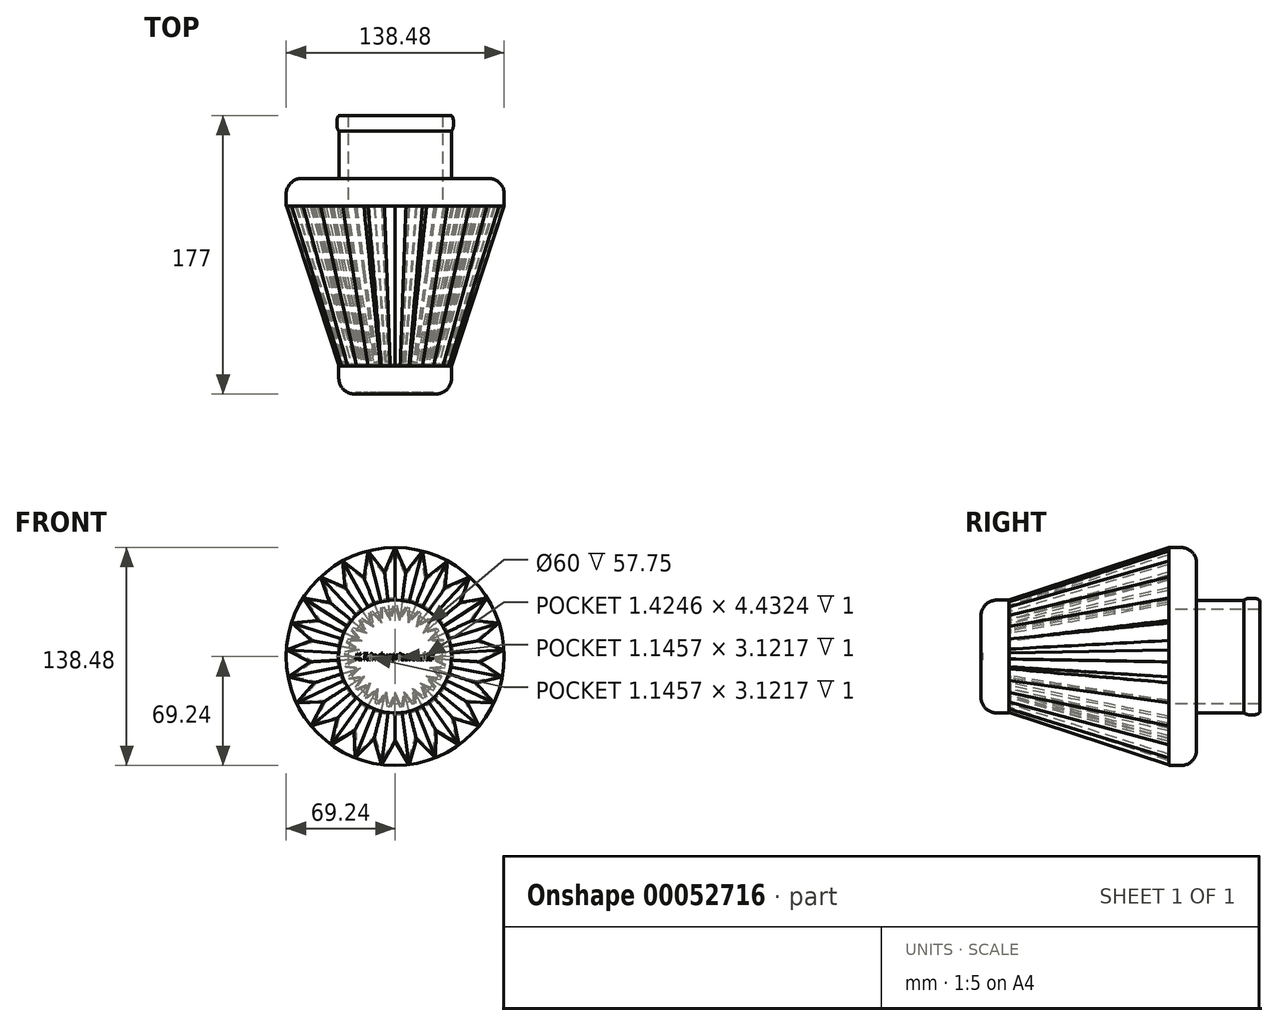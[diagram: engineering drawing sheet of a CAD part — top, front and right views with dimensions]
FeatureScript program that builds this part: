
annotation { "Feature Type Name" : "Feature", "Feature Type Description" : "" }
export const myFeature = defineFeature(function(context is Context, id is Id, definition is map)
    precondition{}
    {
        {
            var Q0;
            Q0=qCreatedBy(makeId("Front.planeOp"),FACE);
            var sketch = newSketch(context, id + "F0", { "sketchPlane" : qUnion([Q0])});
            skLineSegment(sketch, "E0", {"start": v(0, 0) * mm, "end": v(0, 69.24) * mm, "construction": true});
            skLineSegment(sketch, "E1", {"start": v(0, 69.24) * mm, "end": v(-8.68, 49.24) * mm});
            skLineSegment(sketch, "E2", {"start": v(-8.68, 49.24) * mm, "end": v(0, 0) * mm});
            skLineSegment(sketch, "E3.MirrorCS", {"start": v(0, 69.24) * mm, "end": v(8.68, 49.24) * mm});
            skLineSegment(sketch, "E4.MirrorCS", {"start": v(8.68, 49.24) * mm, "end": v(0, 0) * mm});
            skSolve(sketch);
        }
        {
            var Q0;
            Q0=qCreatedBy(makeId("Front.planeOp"),FACE);
            cPlane(context, id + "F1", {"entities" : qUnion([Q0]), "cplaneType" : CPlaneType.OFFSET, "offset" : 101.5 * mm, "width" : 150 * mm, "height" : 150 * mm});
        }
        {
            var Q0;
            Q0=qCreatedBy(id+"F1.planeOp",FACE);
            var sketch = newSketch(context, id + "F2", { "sketchPlane" : qUnion([Q0])});
            skLineSegment(sketch, "E5.0", {"start": v(0, 0) * mm, "end": v(0, 69.24) * mm, "construction": true});
            skLineSegment(sketch, "E6", {"start": v(0, 0) * mm, "end": v(-3.26, 24.79) * mm});
            skLineSegment(sketch, "E7", {"start": v(-3.26, 24.79) * mm, "end": v(0, 35.81) * mm});
            skLineSegment(sketch, "E8.MirrorCS", {"start": v(3.26, 24.79) * mm, "end": v(0, 35.81) * mm});
            skLineSegment(sketch, "E9.MirrorCS", {"start": v(0, 0) * mm, "end": v(3.26, 24.79) * mm});
            skSolve(sketch);
        }
        {
            var Q0;
            Q0=makeQuery(id+"F0.imprint","IMPRINT",FACE,{"disambiguationData":[TD([[makeQuery(id+"F0.imprint","IMPRINT",EDGE,{"derivedFrom":sQuery(id+"F0.wireOp",EDGE,"E1")}),1.0]])]});
            var Q1;
            Q1=makeQuery(id+"F2.imprint","IMPRINT",FACE,{"disambiguationData":[TD([[makeQuery(id+"F2.imprint","IMPRINT",EDGE,{"derivedFrom":sQuery(id+"F2.wireOp",EDGE,"E6")}),-1.0]])]});
            loft(context, id + "F3", {"sheetProfilesArray" : [{ "sheetProfileEntities" : qUnion([Q0]) }, { "sheetProfileEntities" : qUnion([Q1]) }]});
        }
        {
            var Q0;
            Q0=qCreatedBy(makeId("Right.planeOp"),FACE);
            var sketch = newSketch(context, id + "F4", { "sketchPlane" : qUnion([Q0])});
            skLineSegment(sketch, "E10", {"start": v(0, 0) * mm, "end": v(-101.5, 0) * mm, "construction": true});
            skSolve(sketch);
        }
        {
            var Q0;
            Q0=makeQuery(id+"F3.opLoft","SWEPT_BODY",BODY,{"disambiguationData":[OSD([makeQuery(id+"F0.imprint","IMPRINT",FACE,{"disambiguationData":[TD([[makeQuery(id+"F0.imprint","IMPRINT",EDGE,{"derivedFrom":sQuery(id+"F0.wireOp",EDGE,"E1")}),1.0]])]}),makeQuery(id+"F2.imprint","IMPRINT",FACE,{"disambiguationData":[TD([[makeQuery(id+"F2.imprint","IMPRINT",EDGE,{"derivedFrom":sQuery(id+"F2.wireOp",EDGE,"E6")}),-1.0]])]})])]});
            var Q1;
            Q1=makeQuery(id+"F3.opLoft","SWEPT_FACE",FACE,{"disambiguationData":[OSD([sQuery(id+"F0.wireOp",EDGE,"E2"),sQuery(id+"F0.wireOp",EDGE,"E3.MirrorCS"),sQuery(id+"F0.wireOp",EDGE,"E4.MirrorCS"),sQuery(id+"F2.wireOp",EDGE,"E6"),sQuery(id+"F2.wireOp",EDGE,"E8.MirrorCS"),sQuery(id+"F2.wireOp",EDGE,"E9.MirrorCS")])]});
            var Q2;
            Q2=sQuery(id+"F4.wireOp",EDGE,"E10");
            circularPattern(context, id + "F5", {"operationType" : NewBodyOperationType.ADD, "entities" : qUnion([Q0]), "axis" : qUnion([Q2]), "angle" : 360 * degree, "instanceCount" : round(25), "oppositeDirection" : true, "equalSpace" : true});
        }
        {
            var Q0;
            {var subQ0=makeQuery(id+"F3.opLoft","CAP_FACE",FACE,{"disambiguationData":[OSD([makeQuery(id+"F2.imprint","IMPRINT",FACE,{"disambiguationData":[TD([[makeQuery(id+"F2.imprint","IMPRINT",EDGE,{"derivedFrom":sQuery(id+"F2.wireOp",EDGE,"E6")}),-1.0]])]})])],"isStart":true});Q0=makeQuery(id+"F5.boolean.opBoolean","MERGE",FACE,{"derivedFrom":[subQ0,makeQuery(id+"F5.opPattern","COPY",FACE,{"derivedFrom":subQ0,"instanceName":"1"}),makeQuery(id+"F5.opPattern","COPY",FACE,{"derivedFrom":subQ0,"instanceName":"2"}),makeQuery(id+"F5.opPattern","COPY",FACE,{"derivedFrom":subQ0,"instanceName":"3"}),makeQuery(id+"F5.opPattern","COPY",FACE,{"derivedFrom":subQ0,"instanceName":"4"}),makeQuery(id+"F5.opPattern","COPY",FACE,{"derivedFrom":subQ0,"instanceName":"5"}),makeQuery(id+"F5.opPattern","COPY",FACE,{"derivedFrom":subQ0,"instanceName":"6"}),makeQuery(id+"F5.opPattern","COPY",FACE,{"derivedFrom":subQ0,"instanceName":"7"}),makeQuery(id+"F5.opPattern","COPY",FACE,{"derivedFrom":subQ0,"instanceName":"8"}),makeQuery(id+"F5.opPattern","COPY",FACE,{"derivedFrom":subQ0,"instanceName":"9"}),makeQuery(id+"F5.opPattern","COPY",FACE,{"derivedFrom":subQ0,"instanceName":"10"}),makeQuery(id+"F5.opPattern","COPY",FACE,{"derivedFrom":subQ0,"instanceName":"11"}),makeQuery(id+"F5.opPattern","COPY",FACE,{"derivedFrom":subQ0,"instanceName":"12"}),makeQuery(id+"F5.opPattern","COPY",FACE,{"derivedFrom":subQ0,"instanceName":"13"}),makeQuery(id+"F5.opPattern","COPY",FACE,{"derivedFrom":subQ0,"instanceName":"14"}),makeQuery(id+"F5.opPattern","COPY",FACE,{"derivedFrom":subQ0,"instanceName":"15"}),makeQuery(id+"F5.opPattern","COPY",FACE,{"derivedFrom":subQ0,"instanceName":"16"}),makeQuery(id+"F5.opPattern","COPY",FACE,{"derivedFrom":subQ0,"instanceName":"17"}),makeQuery(id+"F5.opPattern","COPY",FACE,{"derivedFrom":subQ0,"instanceName":"18"}),makeQuery(id+"F5.opPattern","COPY",FACE,{"derivedFrom":subQ0,"instanceName":"19"}),makeQuery(id+"F5.opPattern","COPY",FACE,{"derivedFrom":subQ0,"instanceName":"20"}),makeQuery(id+"F5.opPattern","COPY",FACE,{"derivedFrom":subQ0,"instanceName":"21"}),makeQuery(id+"F5.opPattern","COPY",FACE,{"derivedFrom":subQ0,"instanceName":"22"}),makeQuery(id+"F5.opPattern","COPY",FACE,{"derivedFrom":subQ0,"instanceName":"23"}),makeQuery(id+"F5.opPattern","COPY",FACE,{"derivedFrom":subQ0,"instanceName":"24"})]});}
            var Q1;
            {var subQ0=makeQuery(id+"F3.opLoft","CAP_FACE",FACE,{"disambiguationData":[OSD([makeQuery(id+"F0.imprint","IMPRINT",FACE,{"disambiguationData":[TD([[makeQuery(id+"F0.imprint","IMPRINT",EDGE,{"derivedFrom":sQuery(id+"F0.wireOp",EDGE,"E1")}),1.0]])]})])],"isStart":true});Q1=makeQuery(id+"F5.boolean.opBoolean","MERGE",FACE,{"derivedFrom":[subQ0,makeQuery(id+"F5.opPattern","COPY",FACE,{"derivedFrom":subQ0,"instanceName":"1"}),makeQuery(id+"F5.opPattern","COPY",FACE,{"derivedFrom":subQ0,"instanceName":"2"}),makeQuery(id+"F5.opPattern","COPY",FACE,{"derivedFrom":subQ0,"instanceName":"3"}),makeQuery(id+"F5.opPattern","COPY",FACE,{"derivedFrom":subQ0,"instanceName":"4"}),makeQuery(id+"F5.opPattern","COPY",FACE,{"derivedFrom":subQ0,"instanceName":"5"}),makeQuery(id+"F5.opPattern","COPY",FACE,{"derivedFrom":subQ0,"instanceName":"6"}),makeQuery(id+"F5.opPattern","COPY",FACE,{"derivedFrom":subQ0,"instanceName":"7"}),makeQuery(id+"F5.opPattern","COPY",FACE,{"derivedFrom":subQ0,"instanceName":"8"}),makeQuery(id+"F5.opPattern","COPY",FACE,{"derivedFrom":subQ0,"instanceName":"9"}),makeQuery(id+"F5.opPattern","COPY",FACE,{"derivedFrom":subQ0,"instanceName":"10"}),makeQuery(id+"F5.opPattern","COPY",FACE,{"derivedFrom":subQ0,"instanceName":"11"}),makeQuery(id+"F5.opPattern","COPY",FACE,{"derivedFrom":subQ0,"instanceName":"12"}),makeQuery(id+"F5.opPattern","COPY",FACE,{"derivedFrom":subQ0,"instanceName":"13"}),makeQuery(id+"F5.opPattern","COPY",FACE,{"derivedFrom":subQ0,"instanceName":"14"}),makeQuery(id+"F5.opPattern","COPY",FACE,{"derivedFrom":subQ0,"instanceName":"15"}),makeQuery(id+"F5.opPattern","COPY",FACE,{"derivedFrom":subQ0,"instanceName":"16"}),makeQuery(id+"F5.opPattern","COPY",FACE,{"derivedFrom":subQ0,"instanceName":"17"}),makeQuery(id+"F5.opPattern","COPY",FACE,{"derivedFrom":subQ0,"instanceName":"18"}),makeQuery(id+"F5.opPattern","COPY",FACE,{"derivedFrom":subQ0,"instanceName":"19"}),makeQuery(id+"F5.opPattern","COPY",FACE,{"derivedFrom":subQ0,"instanceName":"20"}),makeQuery(id+"F5.opPattern","COPY",FACE,{"derivedFrom":subQ0,"instanceName":"21"}),makeQuery(id+"F5.opPattern","COPY",FACE,{"derivedFrom":subQ0,"instanceName":"22"}),makeQuery(id+"F5.opPattern","COPY",FACE,{"derivedFrom":subQ0,"instanceName":"23"}),makeQuery(id+"F5.opPattern","COPY",FACE,{"derivedFrom":subQ0,"instanceName":"24"})]});}
            shell(context, id + "F6", {"entities" : qUnion([Q0, Q1]), "thickness" : 1 * mm});
        }
        {
            var Q0;
            Q0=qCreatedBy(makeId("Front.planeOp"),FACE);
            var sketch = newSketch(context, id + "F7", { "sketchPlane" : qUnion([Q0])});
            skCircle(sketch, "E11", {"center": v(0, 0) * mm, "radius": 69.24 * mm});
            skCircle(sketch, "E12", {"center": v(0, 0) * mm, "radius": 30 * mm});
            skSolve(sketch);
        }
        {
            var Q0;
            Q0=qSketchRegion(id+"F7",true);
            extrude(context, id + "F8", {"entities" : qUnion([Q0]), "oppositeDirection" : true, "depth" : 17.75 * mm});
        }
        {
            var Q0;
            Q0=qCreatedBy(id+"F1.planeOp",FACE);
            var sketch = newSketch(context, id + "F9", { "sketchPlane" : qUnion([Q0])});
            skCircle(sketch, "E13", {"center": v(0, 0) * mm, "radius": 35.81 * mm});
            skSolve(sketch);
        }
        {
            var Q0;
            Q0=makeQuery(id+"F9.imprint","IMPRINT",FACE,{"disambiguationData":[TD([[makeQuery(id+"F9.imprint","IMPRINT",EDGE,{"derivedFrom":sQuery(id+"F9.wireOp",EDGE,"E13")}),1.0]])]});
            extrude(context, id + "F10", {"entities" : qUnion([Q0]), "depth" : 17.75 * mm});
        }
        {
            var Q0;
            Q0=makeQuery(id+"F8.opExtrude","CAP_FACE",FACE,{"disambiguationData":[OSD([sQuery(id+"F7.wireOp",EDGE,"E11"),sQuery(id+"F7.wireOp",EDGE,"E12")])],"isStart":false});
            var sketch = newSketch(context, id + "F11", { "sketchPlane" : qUnion([Q0])});
            skCircle(sketch, "E14", {"center": v(0, 0) * mm, "radius": 35.76 * mm});
            skSolve(sketch);
        }
        {
            var Q0;
            Q0=makeQuery(id+"F11.imprint","IMPRINT",FACE,{"disambiguationData":[TD([[makeQuery(id+"F11.imprint","IMPRINT",EDGE,{"derivedFrom":sQuery(id+"F11.wireOp",EDGE,"E14")}),1.0]])]});
            extrude(context, id + "F12", {"entities" : qUnion([Q0]), "operationType" : NewBodyOperationType.ADD, "depth" : 35 * mm});
        }
        {
            var Q0;
            Q0=makeQuery(id+"F12.opExtrude","CAP_FACE",FACE,{"disambiguationData":[OSD([sQuery(id+"F7.wireOp",EDGE,"E12"),sQuery(id+"F11.wireOp",EDGE,"E14")])],"isStart":false});
            var sketch = newSketch(context, id + "F13", { "sketchPlane" : qUnion([Q0])});
            skCircle(sketch, "E15", {"center": v(0, 0) * mm, "radius": 37 * mm});
            skSolve(sketch);
        }
        {
            var Q0;
            Q0=makeQuery(id+"F13.imprint","IMPRINT",FACE,{"disambiguationData":[TD([[makeQuery(id+"F13.imprint","IMPRINT",EDGE,{"derivedFrom":sQuery(id+"F13.wireOp",EDGE,"E15")}),1.0]])]});
            extrude(context, id + "F14", {"entities" : qUnion([Q0]), "operationType" : NewBodyOperationType.ADD, "depth" : 10 * mm, "symmetric" : true});
        }
        {
            var Q0;
            Q0=makeQuery(id+"F10.opExtrude","CAP_FACE",FACE,{"disambiguationData":[OSD([sQuery(id+"F9.wireOp",EDGE,"E13")])],"isStart":false});
            var sketch = newSketch(context, id + "F15", { "sketchPlane" : qUnion([Q0])});
            skText(sketch, "E16", { "text": "K.T.industries.co.ltd", "fontName": "OpenSans-Italic.ttf"});
            const initialGuessF15  = {"E16": [-0.02549, -0.00219, 1, 0, 0.0042]};
            skSetInitialGuess(sketch, initialGuessF15);
            skSolve(sketch);
        }
        {
            var Q0;
            Q0=qSketchRegion(id+"F15",true);
            extrude(context, id + "F16", {"entities" : qUnion([Q0]), "operationType" : NewBodyOperationType.REMOVE, "oppositeDirection" : true, "depth" : 1 * mm});
        }
        {
            var Q0;
            Q0=makeQuery(id+"F10.opExtrude","CAP_EDGE",EDGE,{"disambiguationData":[OSD([sQuery(id+"F9.wireOp",EDGE,"E13")])],"isStart":false});
            var Q1;
            Q1=makeQuery(id+"F8.opExtrude","CAP_EDGE",EDGE,{"disambiguationData":[OSD([sQuery(id+"F7.wireOp",EDGE,"E11")])],"isStart":false});
            fillet(context, id + "F17", {"entities" : qUnion([Q0, Q1]), "radius" : 10 * mm, "tangentPropagation" : true, "allowEdgeOverflow" : false});
        }
        {
            var Q0;
            Q0=makeQuery(id+"F14.opExtrude","CAP_EDGE",EDGE,{"disambiguationData":[OSD([sQuery(id+"F13.wireOp",EDGE,"E15")])],"isStart":false});
            var Q1;
            Q1=makeQuery(id+"F14.opExtrude","CAP_EDGE",EDGE,{"disambiguationData":[OSD([sQuery(id+"F13.wireOp",EDGE,"E15")])],"isStart":true});
            fillet(context, id + "F18", {"entities" : qUnion([Q0, Q1]), "radius" : 6 * mm, "tangentPropagation" : true, "allowEdgeOverflow" : false});
        }
        {
            var Q0;
            Q0=makeQuery(id+"F12.opExtrude","CAP_FACE",FACE,{"disambiguationData":[OSD([sQuery(id+"F7.wireOp",EDGE,"E12"),sQuery(id+"F11.wireOp",EDGE,"E14")])],"isStart":false});
            extrude(context, id + "F19", {"entities" : qUnion([Q0]), "operationType" : NewBodyOperationType.ADD, "depth" : 5 * mm});
        }
    });
